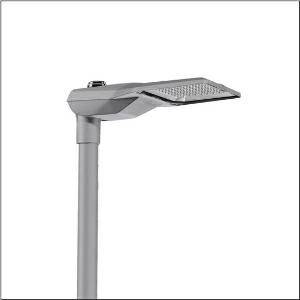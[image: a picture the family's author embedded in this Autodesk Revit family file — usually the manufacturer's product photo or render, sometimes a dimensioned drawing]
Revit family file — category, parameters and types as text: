
# Revit family: streetlight_sl_21_midi___st1_0a_5xe7d27n08mb_7be8
name_source: partatom
category: Lighting Fixtures
units: mm (PartAtom-declared; Revit-internal decimal feet)

## family parameters
Cut with Voids When Loaded = No
Host = Face
Light Source = No
Part Type = Normal
Room Calculation Point = No
Round Connector Dimension = Use Diameter
Shared = No

## types (1)
- --- (1 x LED, 14990 lm, 134.3 W, 2200K)
    Apparent Load = 134 VA
    CIE Flux Codes = 37 72 97 100 100
    Color Rendering = 70
    Color Temperature = 2200K
    Default Elevation = 1800 mm
    Description = Streetlight SL 21 midi, mast luminaire, primary light control with lens, of PMMA, primary optical cover: cover, of toughened safety glass, transparent, light distribution: ST1.0a, light emission: direct distribution, primary light characteristic: asymmetric, installation type: side-entry, LED, 3G 2.5mm², High Power LED, rated luminous flux: 14.990lm, luminous efficacy: 112lm/W, light colour: 722, colour temperature: 2200K, control: overheat protection, presetting dimming linear, constant luminous flux control, time-dependent luminous flux control, flexible luminous flux parameterisation, mains connection: 220..240V, AC, 50/60Hz, connection cable pre-assembled, cable length: 12,5m, wiring characteristics: H05VV-F, start of lifetime: 134W, end of service life: 141W, reduction: 60W, luminaire housing, of diecast aluminium (EN AC-44300), powder-coated, Siteco® metallic grey (DB 702S), corrosivity category C5 mid according to DIN EN ISO 12944, multi-level sealing system, sealing non-destructively replaceable, inclination adjustable: 0°, 5°, 10°, 15°, length: 644mm, width: 335mm, height: 110mm, spigot size: 42mm (side-entry), protection rating (complete): IP66, insulation class (complete): insulation class I (protective earthing), certification: CE, ENEC, ENEC+, VDE, impact resistance: IK09, permissible operating ambient temperature for outdoor applications: -40..+50°C, standard-compliant lighting for roads and squares, packaging unit: 1 piece

Light Distribution: ST1.0a
    Height = 111 mm
    Lamp = 1 x LED
    Lamp Light Flux = 14990 lm
    Lamp Power = 134.3 W
    Lamp count = 1
    Length = 644 mm
    Luminous efficacy = 112 lm/W
    Manufacturer = Siteco
    ModVariant = No
    Model = 5XE7D27N08MB
    Number of Poles = 1
    OnlyDefault = Yes
    Power Factor = 1
    Product Name = Streetlight SL 21 midi | ST1.0a
    Product group = mast luminaire | pylon top
    ProductGroupID = 6100
    Protection Class = Protection class I
    Protection Degree = IP 66
    RLX_Detail_Level = 1
    RLX_Emergency_Light_Flux = 0 lm
    RLX_Emergency_Type = 0
    RLX_Emergency_Type_DB = No
    RlxData = <blob elided: 89797 chars, md5=cb65594a>
    Socket = socket
    Standby Power = 0 W
    System Light Flux = 14991 lm
    System Power = 134 W
    Type Comments = factory setting: luminous flux: 100 % | dim-lin: 254 | 687 mA
    Type Image = l_1294377.jpg
    URL = http://relux.com
    VarID = @adj_085503
    Voltage = 0 V
    Weight = 0.00 kg
    Width = 336 mm

## geometry (parser evidence)
native form markers: Blend x4, Sweep x11
no freeform markers — native parametric forms only
